# Revit family: Utility_Shelf-Bradley_Corp-Mop_Holder_Hooks-Stainless-998x
name_source: partatom
category: Specialty Equipment
revit_build: Autodesk Revit MEP 2012 (Build: 20110309_2315(x64)
units: mm (PartAtom-declared; Revit-internal decimal feet)

## types (4) — shared parameters
ADA Compliant = No
Accessory Material = Metal - Bradley Corp - Stainless Steel-Satin
Assembly Code = C1030320
Buy American Act = To Be Determined
Default Elevation = 48"
Depth = 0"
Height = 0"
Installation Type = Wall Mounted
Length = 0"
Low Emitting Material = No
Manufacturer = Bradley Corporation
MasterFormat Number = 10 57 23
MasterFormat Title = Closet and Utility Shelving
OmniClass Code = 23.21.11.11.11
OmniClass Title = Commercial Storage Shelves
Product Tech Data URL - English = http://bradleycorp.com
Product Tech Data URL - French = http://bradleycorp.com
Product Tech Data URL - Spanish = http://bradleycorp.com
Specifications URL = http://www.bradleycorp.com
URL = http://www.bradleycorp.com
Version = 2.0
Width = 0"
zero-valued in all types: Percentage of Recycled Content

## per-type parameters (varying)
| type | DIM A | DIM B | DIM C | DIM D | DIM E | Description | Holder Spacing |
| 9983 | 30" | 16 3/4" | 12" | 7 1/8" | 8 7/8" | Utility Shelf w/2 Hooks 3 Holders & 1 Drying Rod - 30" W | 3 |
| 9984 BradEX | 36" | 22 7/8" | 10" | 7 1/8" | 8" | Utility Shelf w/3 Hooks 4 Holders & 1 Drying Rod - 36" W | 4 |
| 9985 | 42" | 28 7/8" | 9" | 9" | 7 13/32" | Utility Shelf w/4 Hooks 5 Holders & 1 Drying Rod - 42" W | 5 |
| 9986 | 48" | 34 7/8" | 8 3/8" | 8 3/8" | 7 3/32" | Utility Shelf w/5 Hooks 6 Holders & 1 Drying Rod - 48" W | 6 |

note: column(s) folded — value = type name in every type: Model

## geometry (parser evidence)
native form markers: Blend x6, Sweep x8
no freeform markers — native parametric forms only
